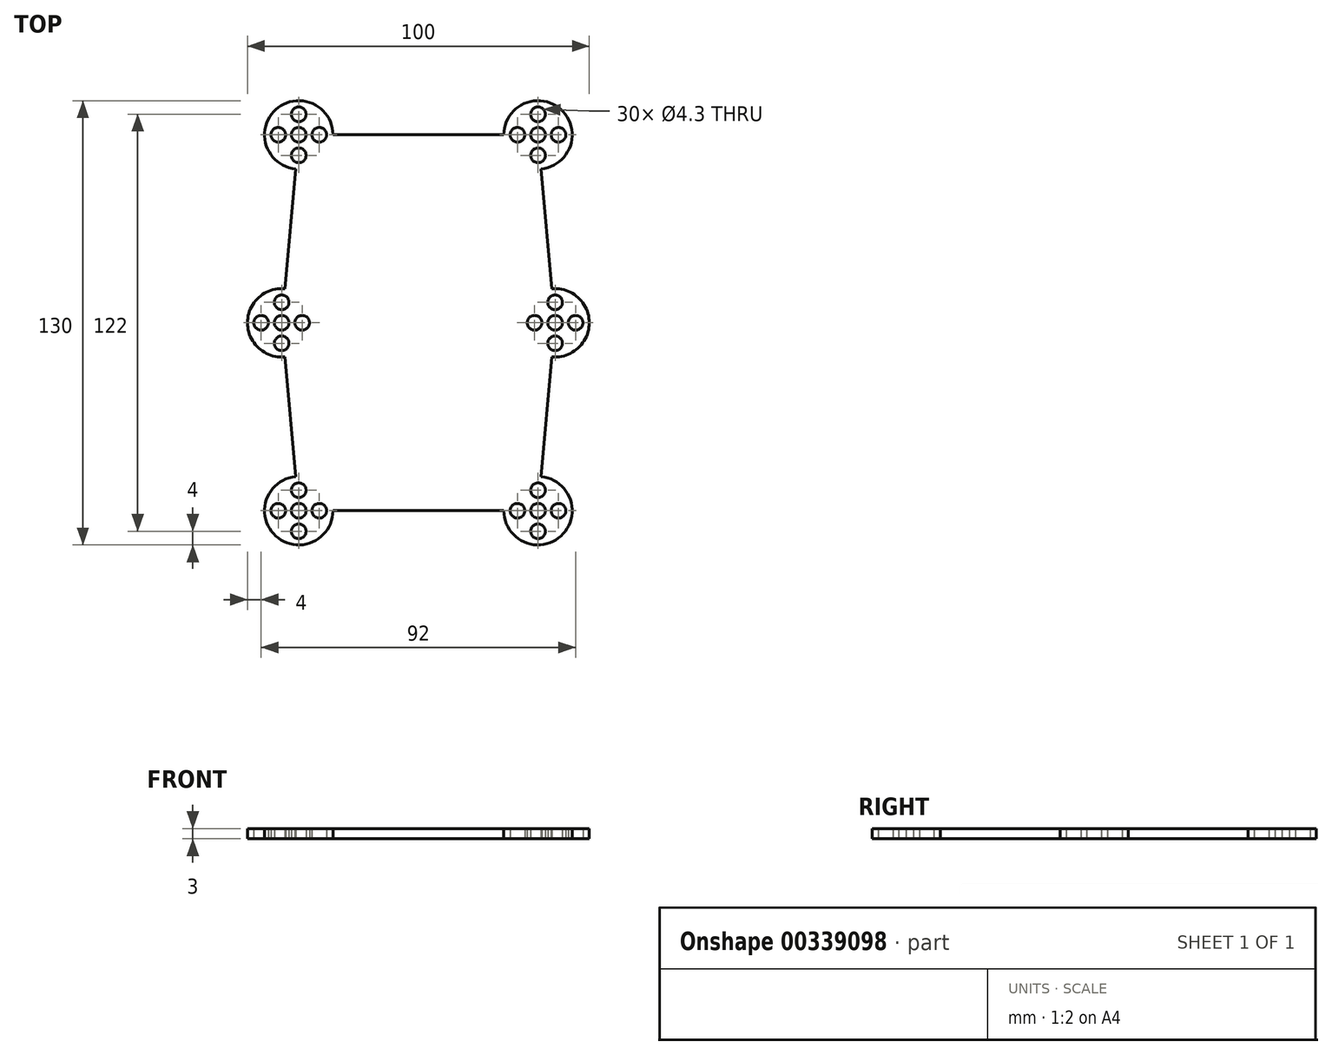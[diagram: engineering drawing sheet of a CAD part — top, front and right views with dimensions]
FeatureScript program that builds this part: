
annotation { "Feature Type Name" : "Feature", "Feature Type Description" : "" }
export const myFeature = defineFeature(function(context is Context, id is Id, definition is map)
    precondition{}
    {
        {
            var Q0;
            Q0=qCreatedBy(makeId("Top.planeOp"),FACE);
            var sketch = newSketch(context, id + "F0", { "sketchPlane" : qUnion([Q0])});
            skPoint(sketch, "E0.middle", {"position": v(0, 0) * mm});
            skCircle(sketch, "E1", {"center": v(-35, 55) * mm, "radius": 2.15 * mm});
            skCircle(sketch, "E2", {"center": v(-35, 49) * mm, "radius": 2.15 * mm});
            skCircle(sketch, "E3", {"center": v(-41, 55) * mm, "radius": 2.15 * mm});
            skCircle(sketch, "E4", {"center": v(-35, 61) * mm, "radius": 2.15 * mm});
            skCircle(sketch, "E5", {"center": v(-29, 55) * mm, "radius": 2.15 * mm});
            skCircle(sketch, "E6", {"center": v(40, 0) * mm, "radius": 2.15 * mm});
            skCircle(sketch, "E7", {"center": v(40, -6) * mm, "radius": 2.15 * mm});
            skCircle(sketch, "E8", {"center": v(34, 0) * mm, "radius": 2.15 * mm});
            skCircle(sketch, "E9", {"center": v(40, 6) * mm, "radius": 2.15 * mm});
            skCircle(sketch, "E10", {"center": v(46, 0) * mm, "radius": 2.15 * mm});
            skPoint(sketch, "E11", {"position": v(50, 0) * mm});
            skCircle(sketch, "E12", {"center": v(-40, 0) * mm, "radius": 2.15 * mm});
            skCircle(sketch, "E13", {"center": v(-40, -6) * mm, "radius": 2.15 * mm});
            skCircle(sketch, "E14", {"center": v(-46, 0) * mm, "radius": 2.15 * mm});
            skCircle(sketch, "E15", {"center": v(-40, 6) * mm, "radius": 2.15 * mm});
            skCircle(sketch, "E16", {"center": v(-34, 0) * mm, "radius": 2.15 * mm});
            skCircle(sketch, "E17", {"center": v(35, 55) * mm, "radius": 2.15 * mm});
            skCircle(sketch, "E18", {"center": v(35, 49) * mm, "radius": 2.15 * mm});
            skCircle(sketch, "E19", {"center": v(29, 55) * mm, "radius": 2.15 * mm});
            skCircle(sketch, "E20", {"center": v(35, 61) * mm, "radius": 2.15 * mm});
            skCircle(sketch, "E21", {"center": v(41, 55) * mm, "radius": 2.15 * mm});
            skCircle(sketch, "E22", {"center": v(35, -55) * mm, "radius": 2.15 * mm});
            skCircle(sketch, "E23", {"center": v(35, -61) * mm, "radius": 2.15 * mm});
            skCircle(sketch, "E24", {"center": v(29, -55) * mm, "radius": 2.15 * mm});
            skCircle(sketch, "E25", {"center": v(35, -49) * mm, "radius": 2.15 * mm});
            skCircle(sketch, "E26", {"center": v(41, -55) * mm, "radius": 2.15 * mm});
            skCircle(sketch, "E27", {"center": v(-35, -55) * mm, "radius": 2.15 * mm});
            skCircle(sketch, "E28", {"center": v(-35, -61) * mm, "radius": 2.15 * mm});
            skCircle(sketch, "E29", {"center": v(-41, -55) * mm, "radius": 2.15 * mm});
            skCircle(sketch, "E30", {"center": v(-35, -49) * mm, "radius": 2.15 * mm});
            skCircle(sketch, "E31", {"center": v(-29, -55) * mm, "radius": 2.15 * mm});
            skArc(sketch, "E32", {"start": v(-25, 55) * mm, "mid": v(-41.74, 62.38) * mm, "end": v(-35.9, 45.04) * mm});
            skArc(sketch, "E33", {"start": v(-39.1, 9.96) * mm, "mid": v(-50, 0) * mm, "end": v(-39.1, -9.96) * mm});
            skArc(sketch, "E34", {"start": v(-35.9, -45.04) * mm, "mid": v(-41.74, -62.38) * mm, "end": v(-25, -55) * mm});
            skArc(sketch, "E35", {"start": v(25, -55) * mm, "mid": v(41.74, -62.38) * mm, "end": v(35.9, -45.04) * mm});
            skArc(sketch, "E36", {"start": v(39.1, -9.96) * mm, "mid": v(50, 0) * mm, "end": v(39.1, 9.96) * mm});
            skArc(sketch, "E37", {"start": v(35.9, 45.04) * mm, "mid": v(41.74, 62.38) * mm, "end": v(25, 55) * mm});
            skLineSegment(sketch, "E38.trimOffspring", {"start": v(-25, 55) * mm, "end": v(25, 55) * mm});
            skLineSegment(sketch, "E39.trimOffspring", {"start": v(-35.9, 45.04) * mm, "end": v(-39.1, 9.96) * mm});
            skPoint(sketch, "E40.orphan", {"position": v(-50, 75) * mm});
            skPoint(sketch, "E41.orphan", {"position": v(50, 75) * mm});
            skPoint(sketch, "E0.top.start.orphan", {"position": v(50, -75) * mm});
            skPoint(sketch, "E0.right.end.orphan", {"position": v(-50, -75) * mm});
            skLineSegment(sketch, "E42.trimOffspring", {"start": v(-25, -55) * mm, "end": v(25, -55) * mm});
            skLineSegment(sketch, "E43.trimOffspring", {"start": v(-35.9, -45.04) * mm, "end": v(-39.1, -9.96) * mm});
            skLineSegment(sketch, "E44.trimOffspring", {"start": v(39.1, -9.96) * mm, "end": v(35.9, -45.04) * mm});
            skLineSegment(sketch, "E45.trimOffspring", {"start": v(35.9, 45.04) * mm, "end": v(39.1, 9.96) * mm});
            skSolve(sketch);
        }
        {
            var Q0;
            Q0 = qSketchRegion(id + "F0", true);
            var Q1;
            Q1=makeQuery(id+"F0.imprint","IMPRINT",FACE,{"disambiguationData":[TD([[makeQuery(id+"F0.imprint","IMPRINT",EDGE,{"derivedFrom":sQuery(id+"F0.wireOp",EDGE,"E1")}),-1.0]])]});
            extrude(context, id + "F1", {"entities" : qUnion([Q0, Q1]), "depth" : 3 * mm});
        }
    });
